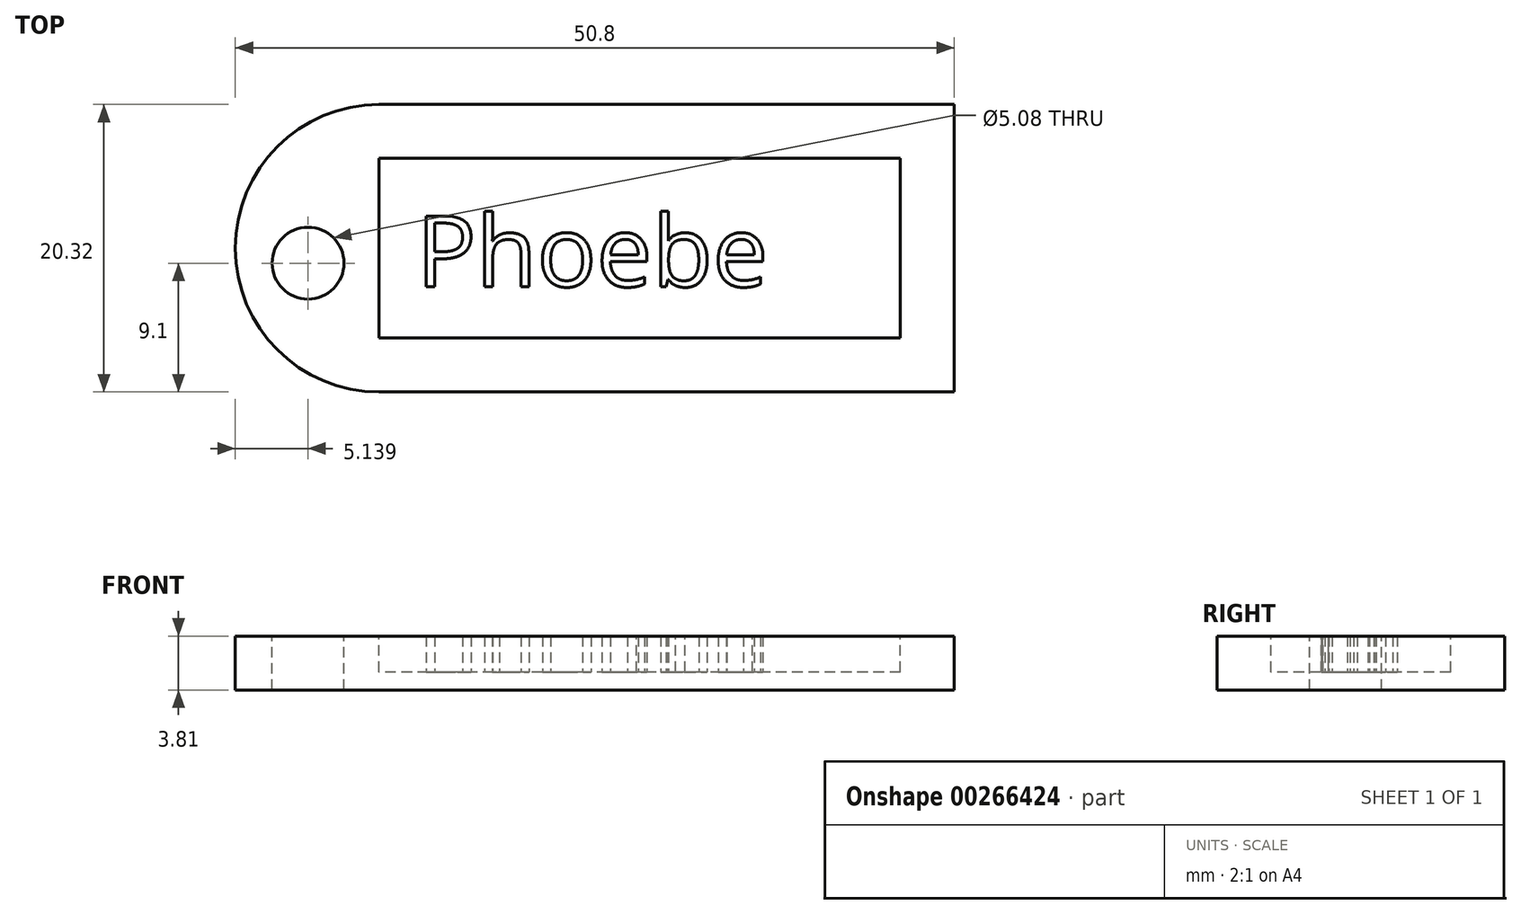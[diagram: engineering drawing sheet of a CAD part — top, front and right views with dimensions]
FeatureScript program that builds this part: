
annotation { "Feature Type Name" : "Feature", "Feature Type Description" : "" }
export const myFeature = defineFeature(function(context is Context, id is Id, definition is map)
    precondition{}
    {
        {
            var Q0;
            Q0=qCreatedBy(makeId("Top.planeOp"),FACE);
            var sketch = newSketch(context, id + "F0", { "sketchPlane" : qUnion([Q0])});
            skLineSegment(sketch, "E0.bottom", {"start": v(-16.85, 40.72) * mm, "end": v(23.8, 40.72) * mm});
            skLineSegment(sketch, "E0.top", {"start": v(-16.85, 20.4) * mm, "end": v(23.8, 20.4) * mm});
            skLineSegment(sketch, "E0.left", {"start": v(-27, 30.56) * mm, "end": v(-27, 30.56) * mm});
            skLineSegment(sketch, "E0.right", {"start": v(23.8, 40.72) * mm, "end": v(23.8, 20.4) * mm});
            skPoint(sketch, "E1.visualSharp", {"position": v(-27, 40.72) * mm});
            skArc(sketch, "E1.filletArc", {"start": v(-16.85, 40.72) * mm, "mid": v(-24.03, 37.75) * mm, "end": v(-27, 30.56) * mm});
            skPoint(sketch, "E2.visualSharp", {"position": v(-27, 20.4) * mm});
            skArc(sketch, "E2.filletArc", {"start": v(-27, 30.56) * mm, "mid": v(-24.03, 23.38) * mm, "end": v(-16.85, 20.4) * mm});
            skSolve(sketch);
        }
        {
            var Q0;
            Q0 = qSketchRegion(id + "F0", true);
            extrude(context, id + "F1", {"entities" : qUnion([Q0]), "depth" : 3.8 * mm});
        }
        {
            var Q0;
            Q0=makeQuery(id+"F1.opExtrude","CAP_FACE",FACE,{"disambiguationData":[OSD([sQuery(id+"F0.wireOp",EDGE,"E0.bottom"),sQuery(id+"F0.wireOp",EDGE,"E0.top"),sQuery(id+"F0.wireOp",EDGE,"E0.right"),sQuery(id+"F0.wireOp",EDGE,"E1.filletArc"),sQuery(id+"F0.wireOp",EDGE,"E2.filletArc")])],"isStart":false});
            var sketch = newSketch(context, id + "F2", { "sketchPlane" : qUnion([Q0])});
            skPoint(sketch, "E3", {"position": v(19.98, 36.91) * mm});
            skPoint(sketch, "E4", {"position": v(-16.85, 24.21) * mm});
            skLineSegment(sketch, "E5.bottom", {"start": v(19.98, 36.91) * mm, "end": v(-16.85, 36.91) * mm});
            skLineSegment(sketch, "E5.top", {"start": v(19.98, 24.21) * mm, "end": v(-16.85, 24.21) * mm});
            skLineSegment(sketch, "E5.left", {"start": v(19.98, 36.91) * mm, "end": v(19.98, 24.21) * mm});
            skLineSegment(sketch, "E5.right", {"start": v(-16.85, 36.91) * mm, "end": v(-16.85, 24.21) * mm});
            skSolve(sketch);
        }
        {
            var Q0;
            Q0 = qSketchRegion(id + "F2", true);
            extrude(context, id + "F3", {"entities" : qUnion([Q0]), "operationType" : NewBodyOperationType.REMOVE, "oppositeDirection" : true, "depth" : 2.54 * mm});
        }
        {
            var Q0;
            Q0=makeQuery(id+"F1.opExtrude","CAP_FACE",FACE,{"disambiguationData":[OSD([sQuery(id+"F0.wireOp",EDGE,"E0.bottom"),sQuery(id+"F0.wireOp",EDGE,"E0.top"),sQuery(id+"F0.wireOp",EDGE,"E0.right"),sQuery(id+"F0.wireOp",EDGE,"E1.filletArc"),sQuery(id+"F0.wireOp",EDGE,"E2.filletArc")])],"isStart":false});
            var sketch = newSketch(context, id + "F4", { "sketchPlane" : qUnion([Q0])});
            skPoint(sketch, "E6", {"position": v(-26.95, 29.5) * mm});
            skPoint(sketch, "E7", {"position": v(-21.87, 29.5) * mm});
            skCircle(sketch, "E8", {"center": v(-21.87, 29.5) * mm, "radius": 2.54 * mm});
            skSolve(sketch);
        }
        {
            var Q0;
            Q0 = qSketchRegion(id + "F4", true);
            extrude(context, id + "F5", {"entities" : qUnion([Q0]), "operationType" : NewBodyOperationType.REMOVE, "oppositeDirection" : true, "depth" : 25.4 * mm});
        }
        {
            var Q0;
            Q0=makeQuery(id+"F3.boolean.opBoolean","COPY",FACE,{"derivedFrom":makeQuery(id+"F3.opExtrude","CAP_FACE",FACE,{"disambiguationData":[OSD([sQuery(id+"F2.wireOp",EDGE,"E5.bottom"),sQuery(id+"F2.wireOp",EDGE,"E5.top"),sQuery(id+"F2.wireOp",EDGE,"E5.left"),sQuery(id+"F2.wireOp",EDGE,"E5.right")])],"isStart":false})});
            var sketch = newSketch(context, id + "F6", { "sketchPlane" : qUnion([Q0])});
            skText(sketch, "E9", { "text": "Phoebe", "fontName": "OpenSans-Regular.ttf"});
            const initialGuessF6  = {"E9": [-0.0142, 0.02785, 1, 0, 0.00503]};
            skSetInitialGuess(sketch, initialGuessF6);
            skSolve(sketch);
        }
        {
            var Q0;
            Q0 = qSketchRegion(id + "F6", true);
            extrude(context, id + "F7", {"entities" : qUnion([Q0]), "operationType" : NewBodyOperationType.ADD, "depth" : 2.54 * mm});
        }
    });
